# Revit family: Toilet-Paper_Holder-Behavioral_Safety_Products-TR740
name_source: partatom
category: Plumbing Fixtures
revit_build: Autodesk Revit 2016 (Build: 20161004_0715(x64)
units: mm (PartAtom-declared; Revit-internal decimal feet)

## family parameters
Cut with Voids When Loaded = No
Host = Face
OmniClass Number = 23.40.20.21
OmniClass Title = Toilet and Bath Specialties
Part Type = Normal
Room Calculation Point = No
Round Connector Dimension = Use Diameter
Shared = No

## types (1)
- Standard
    Buttons = Plastic - Behavioral Safety - Black
    CW Connection = No
    Default Elevation = 0"
    Depth = 8 5/16"
    Description = Recessed Toilet Tissue Holder
    HW Connection = No
    Height = 8 5/16"
    Manufacturer = Behavioral Safety Products
    Manufacturer Fax = 706-705-1191
    Model = TR740
    Product Brochure URL = http://besafeprod.com
    Product Documentation Link = http://besafeprod.com
    Product Page URL = http://besafeprod.com
    Revit Object Download Link = http://library.smartbim.com
    Type Image = <None>
    URL = http://besafeprod.com
    Unit = Metal - Behavioral Safety - White powder coat
    Vent Connection = No
    Waste Connection = No
    Width = 7 7/8"

## geometry (parser evidence)
native form markers: Blend x2, Sweep x5
no freeform markers — native parametric forms only
